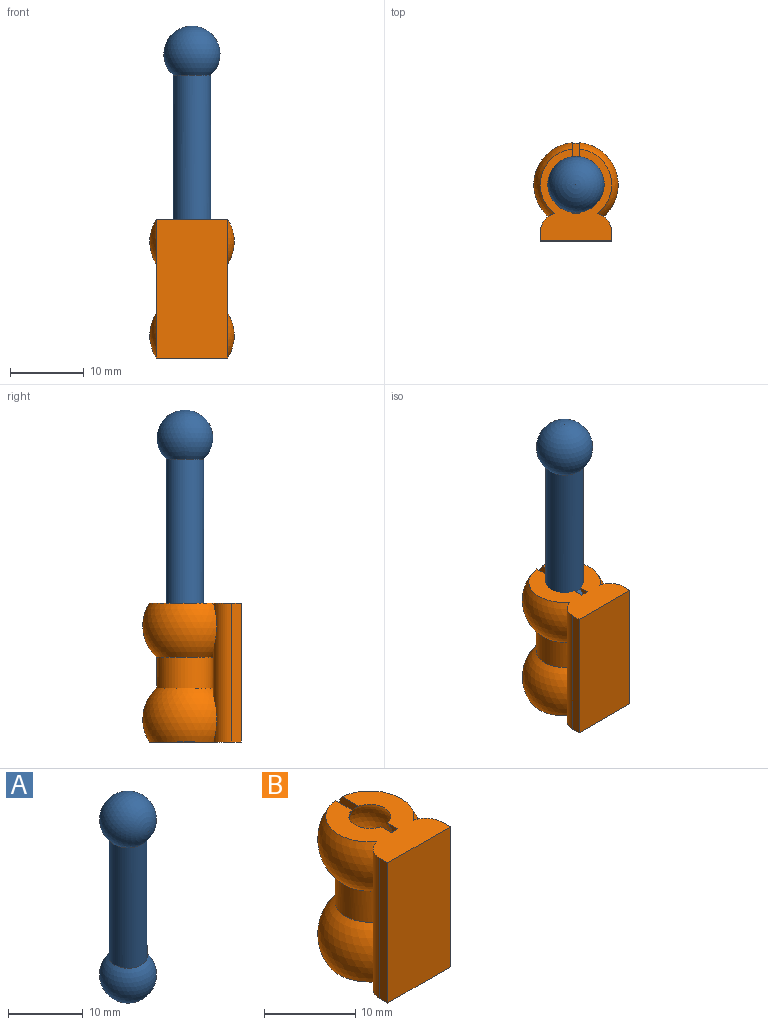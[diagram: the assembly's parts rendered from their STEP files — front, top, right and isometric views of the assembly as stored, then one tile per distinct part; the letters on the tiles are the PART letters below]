
ASSEMBLY  parts=2 mates=1
PART A: 3 faces, bbox 7.6x7.6x33 mm
  f0: cylinder r=2.54mm len=19.72mm, axis (0,0,-1), area 314.7mm2, adj f1,f2
  f1: sphere r=3.81mm, area 159.2mm2, adj f0
  f2: sphere r=3.81mm, area 159.2mm2, adj f0
PART B: 27 faces, bbox 11.4x13.3x18.8 mm
  f0: sphere r=5.71mm, area 203mm2, adj f9,f10,f11,f17,f18,f19,f25,f26
  f1: plane 4.06x1.61mm, normal (1,0,0), area 1.7mm2, adj f2,f8,f18,f20
  f2: plane 1.02x0.2mm, normal (0,0,1), area 0.2mm2, adj f1,f3,f8,f20
  f3: plane 4.06x1.61mm, normal (-1,0,0), area 1.7mm2, adj f2,f8,f18,f20
  f4: sphere r=5.71mm, area 203mm2, adj f13,f14,f15,f16,f17,f19,f25,f26
  f5: plane 1.02x0.2mm, normal (0,0,-1), area 0.2mm2, adj f6,f7,f12,f23
  f6: plane 4.06x1.61mm, normal (1,0,0), area 1.7mm2, adj f5,f12,f13,f23
  f7: plane 4.06x1.61mm, normal (-1,0,0), area 1.7mm2, adj f5,f12,f13,f23
  f8: sphere r=3.81mm, area 154.9mm2, adj f1,f2,f3,f9,f10,f11,f18
  f9: plane 4.06x3.46mm, normal (-1,0,0), area 8.4mm2, adj f0,f8,f10,f18
  f10: plane 1.99x1.02mm, normal (0,0,1), area 2mm2, adj f0,f8,f9,f11
  f11: plane 4.06x3.46mm, normal (1,0,0), area 8.4mm2, adj f0,f8,f10,f18
  f12: sphere r=3.81mm, area 154.9mm2, adj f5,f6,f7,f13,f14,f15,f16
  f13: plane 12.43x9.67mm, normal (0,0,-1), area 82.7mm2, adj f4,f6,f7,f12,f14,f15,f21,f22
  f14: plane 4.06x3.46mm, normal (-1,0,0), area 8.4mm2, adj f4,f12,f13,f16
  f15: plane 4.06x3.46mm, normal (1,0,0), area 8.4mm2, adj f4,f12,f13,f16
  f16: plane 1.99x1.02mm, normal (0,0,-1), area 2mm2, adj f4,f12,f14,f15
  f17: cylinder r=3.81mm len=7.62mm, axis (0,0,1), area 100.1mm2, adj f0,f4
  f18: plane 12.43x9.67mm, normal (0,0,1), area 82.7mm2, adj f0,f1,f3,f8,f9,f11,f20,f21
  f19: plane 5.58x4.59mm, normal (0,1,0), area 21.4mm2, adj f0,f4,f25,f26
  f20: plane 4.06x1.02mm, normal (0,1,0), area 4.1mm2, adj f1,f2,f3,f18
  f21: plane 18.8x1.24mm, normal (-1,0,0), area 23.4mm2, adj f13,f18,f24,f25
  f22: plane 18.8x1.24mm, normal (1,0,0), area 23.4mm2, adj f13,f18,f24,f26
  f23: plane 4.06x1.02mm, normal (0,1,0), area 4.1mm2, adj f5,f6,f7,f13
  f24: plane 18.8x9.67mm, normal (0,-1,0), area 181.7mm2, adj f13,f18,f21,f22
  f25: cylinder r=2.54mm len=18.8mm, axis (0,0,1), area 59.3mm2, adj f0,f4,f13,f18,f19,f21
  f26: cylinder r=2.54mm len=18.8mm, axis (0,0,-1), area 59.3mm2, adj f0,f4,f13,f18,f19,f22
PLACE A rot(axis=(1,0,0),180deg) t=(-1.58,-6.76,38.18)mm
PLACE B rot(axis=(0,1,0),180deg) t=(-1.58,-6.76,12.78)mm fixed
MATE ball B.f17 <-> A.f0  axis (0,0,-1) through (-1.58,-6.76,12.78)mm
